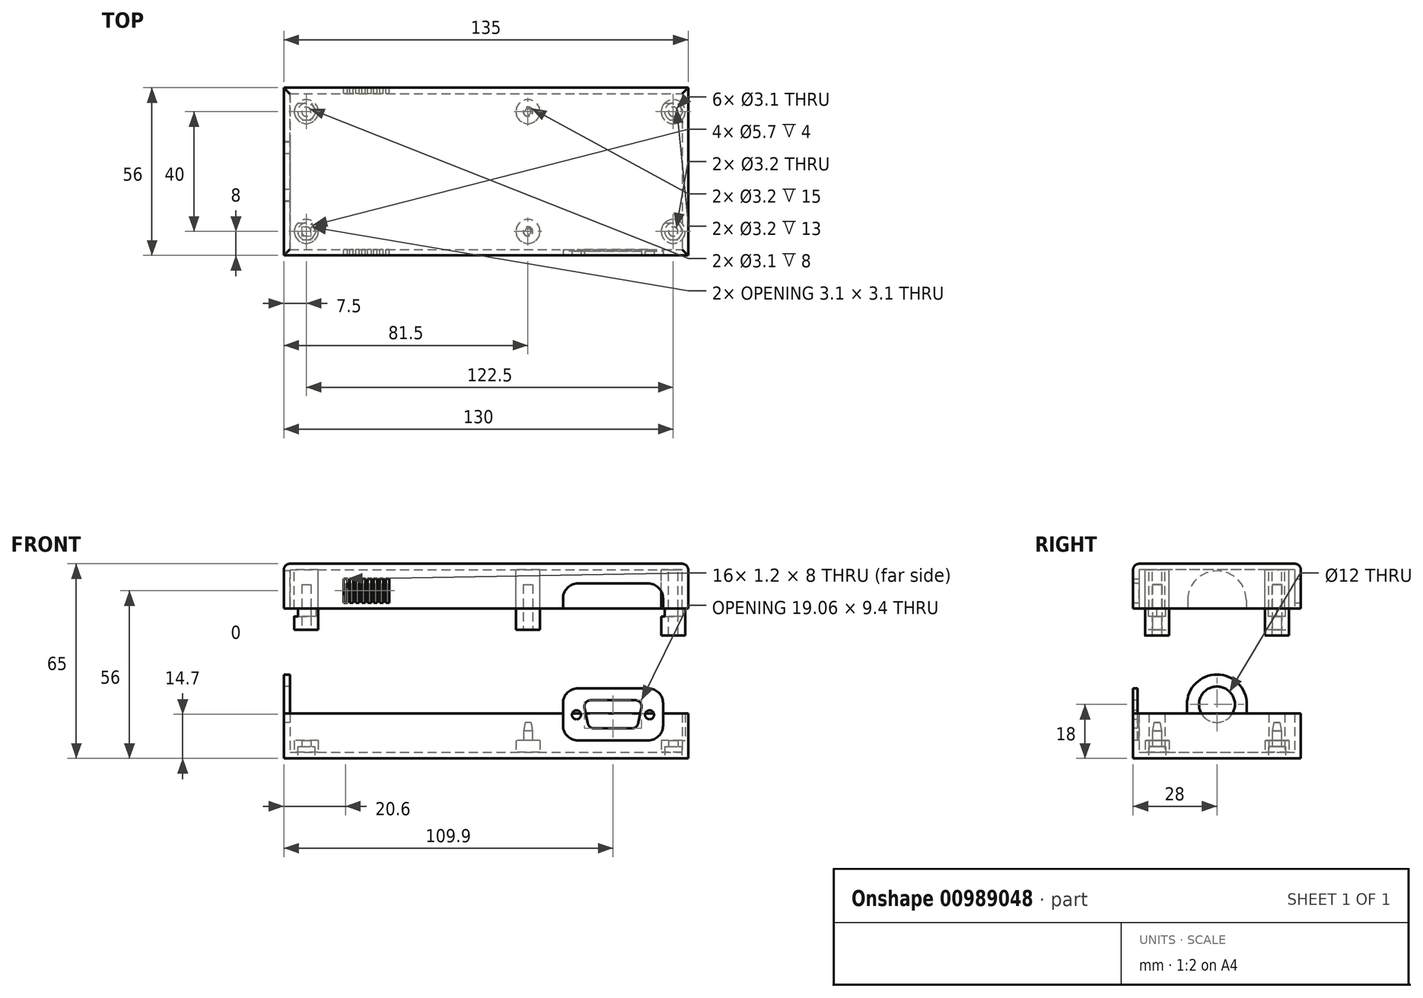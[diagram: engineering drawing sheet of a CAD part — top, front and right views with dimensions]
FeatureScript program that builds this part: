
annotation { "Feature Type Name" : "Feature", "Feature Type Description" : "" }
export const myFeature = defineFeature(function(context is Context, id is Id, definition is map)
    precondition{}
    {
        {
            var Q0;
            Q0=qCreatedBy(makeId("Top.planeOp"),FACE);
            var sketch = newSketch(context, id + "F0", { "sketchPlane" : qUnion([Q0])});
            skLineSegment(sketch, "E0.bottom", {"start": v(0, 0) * mm, "end": v(135, 0) * mm});
            skLineSegment(sketch, "E0.top", {"start": v(0, 56) * mm, "end": v(135, 56) * mm});
            skLineSegment(sketch, "E0.left", {"start": v(0, 0) * mm, "end": v(0, 56) * mm});
            skLineSegment(sketch, "E0.right", {"start": v(135, 0) * mm, "end": v(135, 56) * mm});
            skSolve(sketch);
        }
        {
            var Q0;
            Q0=makeQuery(id+"F0.imprint","IMPRINT",FACE,{"disambiguationData":[TD([[makeQuery(id+"F0.imprint","IMPRINT",EDGE,{"derivedFrom":sQuery(id+"F0.wireOp",EDGE,"E0.bottom")}),1.0]])]});
            extrude(context, id + "F1", {"entities" : qUnion([Q0]), "depth" : 15 * mm, "offsetDistance" : 25 * mm});
        }
        {
            var Q0;
            Q0=makeQuery(id+"F1.opExtrude","CAP_FACE",FACE,{"disambiguationData":[OSD([sQuery(id+"F0.wireOp",EDGE,"E0.bottom"),sQuery(id+"F0.wireOp",EDGE,"E0.top"),sQuery(id+"F0.wireOp",EDGE,"E0.left"),sQuery(id+"F0.wireOp",EDGE,"E0.right")])],"isStart":false});
            shell(context, id + "F2", {"entities" : qUnion([Q0]), "thickness" : 2 * mm});
        }
        {
            var Q0;
            Q0=makeQuery(id+"F2.opShell","OFFSET_FACE",FACE,{"disambiguationData":[OSD([sQuery(id+"F0.wireOp",EDGE,"E0.bottom"),sQuery(id+"F0.wireOp",EDGE,"E0.top"),sQuery(id+"F0.wireOp",EDGE,"E0.left"),sQuery(id+"F0.wireOp",EDGE,"E0.right")])]});
            var sketch = newSketch(context, id + "F3", { "sketchPlane" : qUnion([Q0])});
            skLineSegment(sketch, "E1.bottom", {"start": v(2.5, 53) * mm, "end": v(86.5, 53) * mm, "construction": true});
            skLineSegment(sketch, "E1.top", {"start": v(2.5, 3) * mm, "end": v(86.5, 3) * mm, "construction": true});
            skLineSegment(sketch, "E1.left", {"start": v(2.5, 53) * mm, "end": v(2.5, 3) * mm, "construction": true});
            skLineSegment(sketch, "E1.right", {"start": v(86.5, 53) * mm, "end": v(86.5, 3) * mm, "construction": true});
            skCircle(sketch, "E2", {"center": v(81.5, 48) * mm, "radius": 1.5 * mm});
            skCircle(sketch, "E3", {"center": v(81.5, 8) * mm, "radius": 1.5 * mm});
            skCircle(sketch, "E4", {"center": v(7.5, 8) * mm, "radius": 1.5 * mm});
            skCircle(sketch, "E5", {"center": v(7.5, 48) * mm, "radius": 1.5 * mm});
            skSolve(sketch);
        }
        {
            var Q0;
            Q0=qSketchRegion(id+"F3",true);
            extrude(context, id + "F4", {"entities" : qUnion([Q0]), "operationType" : NewBodyOperationType.ADD, "depth" : 10 * mm, "offsetDistance" : 25 * mm});
        }
        {
            var Q0;
            Q0=makeQuery(id+"F2.opShell","OFFSET_FACE",FACE,{"disambiguationData":[OSD([sQuery(id+"F0.wireOp",EDGE,"E0.bottom"),sQuery(id+"F0.wireOp",EDGE,"E0.top"),sQuery(id+"F0.wireOp",EDGE,"E0.left"),sQuery(id+"F0.wireOp",EDGE,"E0.right")])]});
            var sketch = newSketch(context, id + "F5", { "sketchPlane" : qUnion([Q0])});
            skCircle(sketch, "E6", {"center": v(81.5, 48) * mm, "radius": 4 * mm});
            skCircle(sketch, "E7", {"center": v(81.5, 8) * mm, "radius": 4 * mm});
            skCircle(sketch, "E8", {"center": v(7.5, 48) * mm, "radius": 4 * mm});
            skCircle(sketch, "E9", {"center": v(7.5, 8) * mm, "radius": 4 * mm});
            skSolve(sketch);
        }
        {
            var Q0;
            Q0=qSketchRegion(id+"F5",true);
            extrude(context, id + "F6", {"entities" : qUnion([Q0]), "operationType" : NewBodyOperationType.ADD, "depth" : 4 * mm, "offsetDistance" : 25 * mm});
        }
        {
            var Q0;
            Q0=qCreatedBy(makeId("Top.planeOp"),FACE);
            cPlane(context, id + "F7", {"entities" : qUnion([Q0]), "cplaneType" : CPlaneType.OFFSET, "offset" : 50 * mm, "width" : 150 * mm, "height" : 150 * mm});
        }
        {
            var Q0;
            Q0=makeQuery(id+"F1.opExtrude","SWEPT_FACE",FACE,{"disambiguationData":[OSD([sQuery(id+"F0.wireOp",EDGE,"E0.bottom")])]});
            var sketch = newSketch(context, id + "F8", { "sketchPlane" : qUnion([Q0])});
            skLineSegment(sketch, "E10", {"start": v(102.37, 19.4) * mm, "end": v(117.43, 19.4) * mm});
            skLineSegment(sketch, "E11", {"start": v(119.39, 16.98) * mm, "end": v(118.24, 11.58) * mm});
            skLineSegment(sketch, "E12", {"start": v(116.28, 10) * mm, "end": v(103.52, 10) * mm});
            skLineSegment(sketch, "E13", {"start": v(101.56, 11.58) * mm, "end": v(100.41, 16.98) * mm});
            skPoint(sketch, "E14.visualSharp", {"position": v(99.9, 19.4) * mm});
            skArc(sketch, "E14.filletArc", {"start": v(102.37, 19.4) * mm, "mid": v(100.82, 18.66) * mm, "end": v(100.41, 16.98) * mm});
            skPoint(sketch, "E15.visualSharp", {"position": v(119.9, 19.4) * mm});
            skArc(sketch, "E15.filletArc", {"start": v(119.39, 16.98) * mm, "mid": v(118.98, 18.66) * mm, "end": v(117.43, 19.4) * mm});
            skPoint(sketch, "E16.visualSharp", {"position": v(117.9, 10) * mm});
            skArc(sketch, "E16.filletArc", {"start": v(116.28, 10) * mm, "mid": v(117.54, 10.45) * mm, "end": v(118.24, 11.58) * mm});
            skPoint(sketch, "E17.visualSharp", {"position": v(101.9, 10) * mm});
            skArc(sketch, "E17.filletArc", {"start": v(101.56, 11.58) * mm, "mid": v(102.26, 10.45) * mm, "end": v(103.52, 10) * mm});
            skCircle(sketch, "E18", {"center": v(97.7, 14.53) * mm, "radius": 1.5 * mm});
            skCircle(sketch, "E19", {"center": v(122.1, 14.53) * mm, "radius": 1.5 * mm});
            skLineSegment(sketch, "E20", {"start": v(109.9, 25.37) * mm, "end": v(109.9, 5.82) * mm, "construction": true});
            skLineSegment(sketch, "E21.bottom", {"start": v(98.2, 23.4) * mm, "end": v(121.6, 23.4) * mm});
            skLineSegment(sketch, "E21.top", {"start": v(98.2, 6) * mm, "end": v(121.6, 6) * mm});
            skLineSegment(sketch, "E21.left", {"start": v(93.2, 18.4) * mm, "end": v(93.2, 11) * mm});
            skLineSegment(sketch, "E21.right", {"start": v(126.6, 18.4) * mm, "end": v(126.6, 11) * mm});
            skPoint(sketch, "E22.visualSharp", {"position": v(126.6, 6) * mm});
            skArc(sketch, "E22.filletArc", {"start": v(121.6, 6) * mm, "mid": v(125.14, 7.46) * mm, "end": v(126.6, 11) * mm});
            skPoint(sketch, "E23.visualSharp", {"position": v(93.2, 6) * mm});
            skArc(sketch, "E23.filletArc", {"start": v(93.2, 11) * mm, "mid": v(94.66, 7.46) * mm, "end": v(98.2, 6) * mm});
            skPoint(sketch, "E24.visualSharp", {"position": v(126.6, 23.4) * mm});
            skArc(sketch, "E24.filletArc", {"start": v(126.6, 18.4) * mm, "mid": v(125.14, 21.94) * mm, "end": v(121.6, 23.4) * mm});
            skPoint(sketch, "E25.visualSharp", {"position": v(93.2, 23.4) * mm});
            skArc(sketch, "E25.filletArc", {"start": v(98.2, 23.4) * mm, "mid": v(94.66, 21.94) * mm, "end": v(93.2, 18.4) * mm});
            skSolve(sketch);
        }
        {
            var Q0;
            Q0=makeQuery(id+"F8.imprint","IMPRINT",FACE,{"disambiguationData":[TD([[makeQuery(id+"F8.imprint","IMPRINT",EDGE,{"derivedFrom":sQuery(id+"F8.wireOp",EDGE,"E12")}),1.0]])]});
            var sketch = newSketch(context, id + "F9", { "sketchPlane" : qUnion([Q0])});
            skLineSegment(sketch, "E26.bottom", {"start": v(93.2, 23.4) * mm, "end": v(126.6, 23.4) * mm});
            skLineSegment(sketch, "E26.top", {"start": v(98.2, 6) * mm, "end": v(121.6, 6) * mm});
            skLineSegment(sketch, "E26.left", {"start": v(93.2, 23.4) * mm, "end": v(93.2, 11) * mm});
            skLineSegment(sketch, "E26.right", {"start": v(126.6, 23.4) * mm, "end": v(126.6, 11) * mm});
            skPoint(sketch, "E27.visualSharp", {"position": v(93.2, 6) * mm});
            skArc(sketch, "E27.filletArc", {"start": v(93.2, 11) * mm, "mid": v(94.66, 7.46) * mm, "end": v(98.2, 6) * mm});
            skPoint(sketch, "E28.visualSharp", {"position": v(126.6, 6) * mm});
            skArc(sketch, "E28.filletArc", {"start": v(121.6, 6) * mm, "mid": v(125.14, 7.46) * mm, "end": v(126.6, 11) * mm});
            skSolve(sketch);
        }
        {
            var Q0;
            Q0=qSketchRegion(id+"F9",true);
            extrude(context, id + "F10", {"entities" : qUnion([Q0]), "operationType" : NewBodyOperationType.REMOVE, "oppositeDirection" : true, "depth" : 5 * mm, "offsetDistance" : 25 * mm});
        }
        {
            var Q0;
            Q0=qSketchRegion(id+"F8",true);
            extrude(context, id + "F11", {"entities" : qUnion([Q0]), "oppositeDirection" : true, "depth" : 1.5 * mm, "offsetDistance" : 25 * mm});
        }
        {
            var Q0;
            Q0=makeQuery(id+"F1.opExtrude","SWEPT_FACE",FACE,{"disambiguationData":[OSD([sQuery(id+"F0.wireOp",EDGE,"E0.left")])]});
            var sketch = newSketch(context, id + "F12", { "sketchPlane" : qUnion([Q0])});
            skCircle(sketch, "E29", {"center": v(-28, 18) * mm, "radius": 6 * mm});
            skSolve(sketch);
        }
        {
            var Q0;
            {var subQ0=sQuery(id+"F12.wireOp",EDGE,"E29");var subQ1=makeQuery(id+"F1.opExtrude","CAP_EDGE",EDGE,{"disambiguationData":[OSD([sQuery(id+"F0.wireOp",EDGE,"E0.left")])],"isStart":false});var subQ2=makeQuery(id+"F12.imprint","INTERSECT",VERTEX,{"disambiguationData":[OD(0.0)],"derivedFrom":[subQ1,subQ0]});Q0=makeQuery(id+"F12.imprint","IMPRINT",FACE,{"disambiguationData":[TD([[makeQuery(id+"F12.imprint","IMPRINT",EDGE,{"disambiguationData":[TD([[subQ2,1.0]])],"derivedFrom":subQ0}),1.0]])]});}
            extrude(context, id + "F13", {"entities" : qUnion([Q0]), "operationType" : NewBodyOperationType.REMOVE, "oppositeDirection" : true, "depth" : 25 * mm, "offsetDistance" : 25 * mm});
        }
        {
            var Q0;
            Q0=makeQuery(id+"F1.opExtrude","SWEPT_FACE",FACE,{"disambiguationData":[OSD([sQuery(id+"F0.wireOp",EDGE,"E0.left")])]});
            var sketch = newSketch(context, id + "F14", { "sketchPlane" : qUnion([Q0])});
            skCircle(sketch, "E30", {"center": v(-28, 18) * mm, "radius": 6 * mm});
            skArc(sketch, "E31", {"start": v(-18, 18) * mm, "mid": v(-28, 28) * mm, "end": v(-38, 18) * mm});
            skLineSegment(sketch, "E32.top", {"start": v(-38, 8) * mm, "end": v(-18, 8) * mm});
            skLineSegment(sketch, "E32.left", {"start": v(-38, 18) * mm, "end": v(-38, 8) * mm});
            skLineSegment(sketch, "E32.right", {"start": v(-18, 18) * mm, "end": v(-18, 8) * mm});
            skSolve(sketch);
        }
        {
            var Q0;
            {var subQ0=sQuery(id+"F14.wireOp",EDGE,"E30");var subQ1=sQuery(id+"F0.wireOp",EDGE,"E0.bottom");var subQ2=sQuery(id+"F0.wireOp",EDGE,"E0.left");var subQ7=makeQuery(id+"F1.opExtrude","CAP_EDGE",EDGE,{"disambiguationData":[OSD([subQ2])],"isStart":false});var subQ8=makeQuery(id+"F13.boolean.opBoolean","SPLIT",EDGE,{"disambiguationData":[TD([makeQuery(id+"F1.opExtrude","SWEPT_FACE",FACE,{"disambiguationData":[OSD([subQ1])]})])],"derivedFrom":subQ7});var subQ9=makeQuery(id+"F14.imprint","INTERSECT",VERTEX,{"derivedFrom":[subQ8,subQ0]});Q0=makeQuery(id+"F14.imprint","IMPRINT",FACE,{"disambiguationData":[TD([[makeQuery(id+"F14.imprint","IMPRINT",EDGE,{"disambiguationData":[TD([[subQ9,-1.0]])],"derivedFrom":subQ0}),-1.0]])]});}
            extrude(context, id + "F15", {"entities" : qUnion([Q0]), "operationType" : NewBodyOperationType.ADD, "oppositeDirection" : true, "depth" : 2 * mm, "offsetDistance" : 25 * mm});
        }
        {
            var Q0;
            Q0=qCreatedBy(id+"F7.planeOp",FACE);
            var sketch = newSketch(context, id + "F16", { "sketchPlane" : qUnion([Q0])});
            skLineSegment(sketch, "E33.bottom", {"start": v(0, 56) * mm, "end": v(135, 56) * mm});
            skLineSegment(sketch, "E33.top", {"start": v(0, 0) * mm, "end": v(135, 0) * mm});
            skLineSegment(sketch, "E33.left", {"start": v(0, 56) * mm, "end": v(0, 0) * mm});
            skLineSegment(sketch, "E33.right", {"start": v(135, 56) * mm, "end": v(135, 0) * mm});
            skSolve(sketch);
        }
        {
            var Q0;
            Q0=makeQuery(id+"F16.imprint","IMPRINT",FACE,{"disambiguationData":[TD([[makeQuery(id+"F16.imprint","IMPRINT",EDGE,{"derivedFrom":sQuery(id+"F16.wireOp",EDGE,"E33.bottom")}),-1.0]])]});
            extrude(context, id + "F17", {"entities" : qUnion([Q0]), "depth" : 15 * mm, "offsetDistance" : 25 * mm});
        }
        {
            var Q0;
            Q0=makeQuery(id+"F17.opExtrude","CAP_FACE",FACE,{"disambiguationData":[OSD([sQuery(id+"F16.wireOp",EDGE,"E33.bottom"),sQuery(id+"F16.wireOp",EDGE,"E33.top"),sQuery(id+"F16.wireOp",EDGE,"E33.left"),sQuery(id+"F16.wireOp",EDGE,"E33.right")])],"isStart":true});
            shell(context, id + "F18", {"entities" : qUnion([Q0]), "thickness" : 2 * mm});
        }
        {
            var Q0;
            Q0=makeQuery(id+"F17.opExtrude","SWEPT_FACE",FACE,{"disambiguationData":[OSD([sQuery(id+"F16.wireOp",EDGE,"E33.left")])]});
            var sketch = newSketch(context, id + "F19", { "sketchPlane" : qUnion([Q0])});
            skArc(sketch, "E34", {"start": v(-18.2, 52.8) * mm, "mid": v(-28, 62.6) * mm, "end": v(-37.8, 52.8) * mm});
            skPoint(sketch, "E34.centerSnap0", {"position": v(-28, 50) * mm});
            skLineSegment(sketch, "E35.top", {"start": v(-37.8, 43) * mm, "end": v(-18.2, 43) * mm});
            skLineSegment(sketch, "E35.left", {"start": v(-37.8, 52.8) * mm, "end": v(-37.8, 43) * mm});
            skLineSegment(sketch, "E35.right", {"start": v(-18.2, 52.8) * mm, "end": v(-18.2, 43) * mm});
            skSolve(sketch);
        }
        {
            var Q0;
            {var subQ0=sQuery(id+"F19.wireOp",EDGE,"E34");var subQ1=makeQuery(id+"F17.opExtrude","CAP_EDGE",EDGE,{"disambiguationData":[OSD([sQuery(id+"F16.wireOp",EDGE,"E33.left")])],"isStart":true});var subQ2=makeQuery(id+"F19.imprint","INTERSECT",VERTEX,{"disambiguationData":[OD(0.0)],"derivedFrom":[subQ1,subQ0]});Q0=makeQuery(id+"F19.imprint","IMPRINT",FACE,{"disambiguationData":[TD([[makeQuery(id+"F19.imprint","IMPRINT",EDGE,{"disambiguationData":[TD([[subQ2,1.0]])],"derivedFrom":subQ0}),1.0]])]});}
            extrude(context, id + "F20", {"entities" : qUnion([Q0]), "operationType" : NewBodyOperationType.REMOVE, "oppositeDirection" : true, "depth" : 5 * mm, "offsetDistance" : 25 * mm});
        }
        {
            var Q0;
            Q0=makeQuery(id+"F17.opExtrude","SWEPT_FACE",FACE,{"disambiguationData":[OSD([sQuery(id+"F16.wireOp",EDGE,"E33.top")])]});
            var sketch = newSketch(context, id + "F21", { "sketchPlane" : qUnion([Q0])});
            skLineSegment(sketch, "E36.bottom", {"start": v(93.2, 50) * mm, "end": v(126.6, 50) * mm});
            skLineSegment(sketch, "E36.top", {"start": v(98.2, 58.4) * mm, "end": v(121.6, 58.4) * mm});
            skLineSegment(sketch, "E36.left", {"start": v(93.2, 50) * mm, "end": v(93.2, 53.4) * mm});
            skLineSegment(sketch, "E36.right", {"start": v(126.6, 50) * mm, "end": v(126.6, 53.4) * mm});
            skPoint(sketch, "E37.visualSharp", {"position": v(93.2, 58.4) * mm});
            skArc(sketch, "E37.filletArc", {"start": v(98.2, 58.4) * mm, "mid": v(94.66, 56.94) * mm, "end": v(93.2, 53.4) * mm});
            skPoint(sketch, "E38.visualSharp", {"position": v(126.6, 58.4) * mm});
            skArc(sketch, "E38.filletArc", {"start": v(126.6, 53.4) * mm, "mid": v(125.14, 56.94) * mm, "end": v(121.6, 58.4) * mm});
            skSolve(sketch);
        }
        {
            var Q0;
            Q0=makeQuery(id+"F21.imprint","IMPRINT",FACE,{"disambiguationData":[TD([[makeQuery(id+"F21.imprint","IMPRINT",EDGE,{"derivedFrom":sQuery(id+"F21.wireOp",EDGE,"E36.bottom")}),1.0]])]});
            extrude(context, id + "F22", {"entities" : qUnion([Q0]), "operationType" : NewBodyOperationType.REMOVE, "oppositeDirection" : true, "depth" : 5 * mm, "offsetDistance" : 25 * mm});
        }
        {
            var Q0;
            Q0=makeQuery(id+"F17.opExtrude","CAP_FACE",FACE,{"disambiguationData":[OSD([sQuery(id+"F16.wireOp",EDGE,"E33.bottom"),sQuery(id+"F16.wireOp",EDGE,"E33.top"),sQuery(id+"F16.wireOp",EDGE,"E33.left"),sQuery(id+"F16.wireOp",EDGE,"E33.right")])],"isStart":false});
            fillet(context, id + "F23", {"entities" : qUnion([Q0]), "radius" : 2 * mm, "tangentPropagation" : true, "allowEdgeOverflow" : false});
        }
        {
            var Q0;
            Q0=makeQuery(id+"F18.opShell","OFFSET_FACE",FACE,{"disambiguationData":[OSD([sQuery(id+"F16.wireOp",EDGE,"E33.bottom"),sQuery(id+"F16.wireOp",EDGE,"E33.top"),sQuery(id+"F16.wireOp",EDGE,"E33.left"),sQuery(id+"F16.wireOp",EDGE,"E33.right")])]});
            var sketch = newSketch(context, id + "F24", { "sketchPlane" : qUnion([Q0])});
            skCircle(sketch, "E39", {"center": v(81.5, -48) * mm, "radius": 4 * mm});
            skCircle(sketch, "E40", {"center": v(81.5, -8) * mm, "radius": 4 * mm});
            skCircle(sketch, "E41", {"center": v(7.5, -48) * mm, "radius": 4 * mm});
            skCircle(sketch, "E42", {"center": v(7.5, -8) * mm, "radius": 4 * mm});
            skSolve(sketch);
        }
        {
            var Q0;
            Q0 = qSketchRegion(id + "F24", true);
            extrude(context, id + "F25", {"entities" : qUnion([Q0]), "operationType" : NewBodyOperationType.ADD, "depth" : 20 * mm, "offsetDistance" : 25 * mm});
        }
        {
            var Q0;
            Q0=makeQuery(id+"F25.opExtrude","CAP_FACE",FACE,{"disambiguationData":[OSD([sQuery(id+"F24.wireOp",EDGE,"E40")])],"isStart":false});
            var sketch = newSketch(context, id + "F26", { "sketchPlane" : qUnion([Q0])});
            skCircle(sketch, "E43", {"center": v(81.5, -8) * mm, "radius": 1.6 * mm});
            skCircle(sketch, "E44", {"center": v(7.5, -8) * mm, "radius": 1.55 * mm});
            skCircle(sketch, "E45", {"center": v(7.5, -48) * mm, "radius": 1.55 * mm});
            skCircle(sketch, "E46", {"center": v(81.5, -48) * mm, "radius": 1.6 * mm});
            skSolve(sketch);
        }
        {
            var Q0;
            Q0 = qSketchRegion(id + "F26", true);
            extrude(context, id + "F27", {"entities" : qUnion([Q0]), "operationType" : NewBodyOperationType.REMOVE, "oppositeDirection" : true, "depth" : 15 * mm, "offsetDistance" : 25 * mm});
        }
        {
            var Q0;
            Q0=makeQuery(id+"F17.opExtrude","SWEPT_FACE",FACE,{"disambiguationData":[OSD([sQuery(id+"F16.wireOp",EDGE,"E33.bottom")])]});
            var sketch = newSketch(context, id + "F28", { "sketchPlane" : qUnion([Q0])});
            skLineSegment(sketch, "E47.bottom", {"start": v(-21.2, 60) * mm, "end": v(-20, 60) * mm});
            skLineSegment(sketch, "E47.top", {"start": v(-21.2, 52) * mm, "end": v(-20, 52) * mm});
            skLineSegment(sketch, "E47.left", {"start": v(-21.2, 60) * mm, "end": v(-21.2, 52) * mm});
            skLineSegment(sketch, "E47.right", {"start": v(-20, 60) * mm, "end": v(-20, 52) * mm});
            skLineSegment(sketch, "E48.1.0.0", {"start": v(-23.2, 60) * mm, "end": v(-23.2, 52) * mm});
            skLineSegment(sketch, "E48.1.0.1", {"start": v(-22, 60) * mm, "end": v(-22, 52) * mm});
            skLineSegment(sketch, "E48.1.0.2", {"start": v(-23.2, 52) * mm, "end": v(-22, 52) * mm});
            skLineSegment(sketch, "E48.1.0.3", {"start": v(-23.2, 60) * mm, "end": v(-22, 60) * mm});
            skLineSegment(sketch, "E48.2.0.0", {"start": v(-25.2, 60) * mm, "end": v(-25.2, 52) * mm});
            skLineSegment(sketch, "E48.2.0.1", {"start": v(-24, 60) * mm, "end": v(-24, 52) * mm});
            skLineSegment(sketch, "E48.2.0.2", {"start": v(-25.2, 52) * mm, "end": v(-24, 52) * mm});
            skLineSegment(sketch, "E48.2.0.3", {"start": v(-25.2, 60) * mm, "end": v(-24, 60) * mm});
            skLineSegment(sketch, "E48.3.0.0", {"start": v(-27.2, 60) * mm, "end": v(-27.2, 52) * mm});
            skLineSegment(sketch, "E48.3.0.1", {"start": v(-26, 60) * mm, "end": v(-26, 52) * mm});
            skLineSegment(sketch, "E48.3.0.2", {"start": v(-27.2, 52) * mm, "end": v(-26, 52) * mm});
            skLineSegment(sketch, "E48.3.0.3", {"start": v(-27.2, 60) * mm, "end": v(-26, 60) * mm});
            skLineSegment(sketch, "E48.4.0.0", {"start": v(-29.2, 60) * mm, "end": v(-29.2, 52) * mm});
            skLineSegment(sketch, "E48.4.0.1", {"start": v(-28, 60) * mm, "end": v(-28, 52) * mm});
            skLineSegment(sketch, "E48.4.0.2", {"start": v(-29.2, 52) * mm, "end": v(-28, 52) * mm});
            skLineSegment(sketch, "E48.4.0.3", {"start": v(-29.2, 60) * mm, "end": v(-28, 60) * mm});
            skLineSegment(sketch, "E48.5.0.0", {"start": v(-31.2, 60) * mm, "end": v(-31.2, 52) * mm});
            skLineSegment(sketch, "E48.5.0.1", {"start": v(-30, 60) * mm, "end": v(-30, 52) * mm});
            skLineSegment(sketch, "E48.5.0.2", {"start": v(-31.2, 52) * mm, "end": v(-30, 52) * mm});
            skLineSegment(sketch, "E48.5.0.3", {"start": v(-31.2, 60) * mm, "end": v(-30, 60) * mm});
            skLineSegment(sketch, "E48.6.0.0", {"start": v(-33.2, 60) * mm, "end": v(-33.2, 52) * mm});
            skLineSegment(sketch, "E48.6.0.1", {"start": v(-32, 60) * mm, "end": v(-32, 52) * mm});
            skLineSegment(sketch, "E48.6.0.2", {"start": v(-33.2, 52) * mm, "end": v(-32, 52) * mm});
            skLineSegment(sketch, "E48.6.0.3", {"start": v(-33.2, 60) * mm, "end": v(-32, 60) * mm});
            skLineSegment(sketch, "E48.7.0.0", {"start": v(-35.2, 60) * mm, "end": v(-35.2, 52) * mm});
            skLineSegment(sketch, "E48.7.0.1", {"start": v(-34, 60) * mm, "end": v(-34, 52) * mm});
            skLineSegment(sketch, "E48.7.0.2", {"start": v(-35.2, 52) * mm, "end": v(-34, 52) * mm});
            skLineSegment(sketch, "E48.7.0.3", {"start": v(-35.2, 60) * mm, "end": v(-34, 60) * mm});
            skLineSegment(sketch, "E48.direction1", {"start": v(-21.2, 52) * mm, "end": v(-23.2, 52) * mm, "construction": true});
            skSolve(sketch);
        }
        {
            var Q0;
            Q0 = qSketchRegion(id + "F28", true);
            extrude(context, id + "F29", {"entities" : qUnion([Q0]), "operationType" : NewBodyOperationType.REMOVE, "oppositeDirection" : true, "depth" : 100 * mm, "offsetDistance" : 25 * mm});
        }
        {
            var Q0;
            Q0=makeQuery(id+"F1.opExtrude","CAP_FACE",FACE,{"disambiguationData":[OSD([sQuery(id+"F0.wireOp",EDGE,"E0.bottom"),sQuery(id+"F0.wireOp",EDGE,"E0.top"),sQuery(id+"F0.wireOp",EDGE,"E0.left"),sQuery(id+"F0.wireOp",EDGE,"E0.right")])],"isStart":true});
            var sketch = newSketch(context, id + "F30", { "sketchPlane" : qUnion([Q0])});
            skCircle(sketch, "E49", {"center": v(7.5, -48) * mm, "radius": 1.55 * mm});
            skCircle(sketch, "E50", {"center": v(7.5, -8) * mm, "radius": 1.55 * mm});
            skCircle(sketch, "E51", {"center": v(130, -48) * mm, "radius": 1.55 * mm});
            skCircle(sketch, "E52", {"center": v(130, -8) * mm, "radius": 1.55 * mm});
            skSolve(sketch);
        }
        {
            var Q0;
            Q0=makeQuery(id+"F2.opShell","OFFSET_FACE",FACE,{"disambiguationData":[OSD([sQuery(id+"F0.wireOp",EDGE,"E0.bottom"),sQuery(id+"F0.wireOp",EDGE,"E0.top"),sQuery(id+"F0.wireOp",EDGE,"E0.left"),sQuery(id+"F0.wireOp",EDGE,"E0.right")])]});
            var sketch = newSketch(context, id + "F31", { "sketchPlane" : qUnion([Q0])});
            skCircle(sketch, "E53", {"center": v(130, 48) * mm, "radius": 4 * mm});
            skCircle(sketch, "E54", {"center": v(130, 8) * mm, "radius": 4 * mm});
            skSolve(sketch);
        }
        {
            var Q0;
            Q0 = qSketchRegion(id + "F31", true);
            extrude(context, id + "F32", {"entities" : qUnion([Q0]), "operationType" : NewBodyOperationType.ADD, "depth" : 4 * mm, "offsetDistance" : 25 * mm});
        }
        {
            var Q0;
            Q0 = qSketchRegion(id + "F30", true);
            extrude(context, id + "F33", {"entities" : qUnion([Q0]), "operationType" : NewBodyOperationType.REMOVE, "oppositeDirection" : true, "depth" : 25 * mm, "offsetDistance" : 25 * mm});
        }
        {
            var Q0;
            Q0=makeQuery(id+"F1.opExtrude","CAP_FACE",FACE,{"disambiguationData":[OSD([sQuery(id+"F0.wireOp",EDGE,"E0.bottom"),sQuery(id+"F0.wireOp",EDGE,"E0.top"),sQuery(id+"F0.wireOp",EDGE,"E0.left"),sQuery(id+"F0.wireOp",EDGE,"E0.right")])],"isStart":true});
            var sketch = newSketch(context, id + "F34", { "sketchPlane" : qUnion([Q0])});
            skCircle(sketch, "E55", {"center": v(7.5, -8) * mm, "radius": 2.85 * mm});
            skCircle(sketch, "E56", {"center": v(7.5, -48) * mm, "radius": 2.85 * mm});
            skCircle(sketch, "E57", {"center": v(130, -8) * mm, "radius": 2.85 * mm});
            skCircle(sketch, "E58", {"center": v(130, -48) * mm, "radius": 2.85 * mm});
            skSolve(sketch);
        }
        {
            var Q0;
            Q0 = qSketchRegion(id + "F34", true);
            extrude(context, id + "F35", {"entities" : qUnion([Q0]), "operationType" : NewBodyOperationType.REMOVE, "oppositeDirection" : true, "depth" : 4 * mm, "offsetDistance" : 25 * mm});
        }
        {
            var Q0;
            Q0=makeQuery(id+"F18.opShell","OFFSET_FACE",FACE,{"disambiguationData":[OSD([sQuery(id+"F16.wireOp",EDGE,"E33.bottom"),sQuery(id+"F16.wireOp",EDGE,"E33.top"),sQuery(id+"F16.wireOp",EDGE,"E33.left"),sQuery(id+"F16.wireOp",EDGE,"E33.right")])]});
            var sketch = newSketch(context, id + "F36", { "sketchPlane" : qUnion([Q0])});
            skCircle(sketch, "E59", {"center": v(130, -8) * mm, "radius": 4 * mm});
            skCircle(sketch, "E60", {"center": v(130, -48) * mm, "radius": 4 * mm});
            skSolve(sketch);
        }
        {
            var Q0;
            Q0 = qSketchRegion(id + "F36", true);
            extrude(context, id + "F37", {"entities" : qUnion([Q0]), "operationType" : NewBodyOperationType.ADD, "depth" : 22 * mm, "offsetDistance" : 25 * mm});
        }
        {
            var Q0;
            Q0=makeQuery(id+"F32.opExtrude","CAP_FACE",FACE,{"disambiguationData":[OSD([sQuery(id+"F31.wireOp",EDGE,"E53")])],"isStart":false});
            var sketch = newSketch(context, id + "F38", { "sketchPlane" : qUnion([Q0])});
            skCircle(sketch, "E61", {"center": v(130, 48) * mm, "radius": 4 * mm});
            skCircle(sketch, "E62", {"center": v(130, 8) * mm, "radius": 4 * mm});
            skSolve(sketch);
        }
        {
            var Q0;
            Q0 = qSketchRegion(id + "F38", true);
            extrude(context, id + "F39", {"entities" : qUnion([Q0]), "operationType" : NewBodyOperationType.REMOVE, "depth" : 25 * mm, "offsetDistance" : 25 * mm});
        }
        {
            var Q0;
            Q0=makeQuery(id+"F18.opShell","OFFSET_FACE",FACE,{"disambiguationData":[OSD([sQuery(id+"F16.wireOp",EDGE,"E33.bottom"),sQuery(id+"F16.wireOp",EDGE,"E33.top"),sQuery(id+"F16.wireOp",EDGE,"E33.left"),sQuery(id+"F16.wireOp",EDGE,"E33.right")])]});
            var sketch = newSketch(context, id + "F40", { "sketchPlane" : qUnion([Q0])});
            skCircle(sketch, "E63", {"center": v(130, -8) * mm, "radius": 1.6 * mm});
            skCircle(sketch, "E64", {"center": v(130, -48) * mm, "radius": 1.6 * mm});
            skSolve(sketch);
        }
        {
            var Q0;
            Q0 = qSketchRegion(id + "F40", true);
            extrude(context, id + "F41", {"entities" : qUnion([Q0]), "operationType" : NewBodyOperationType.REMOVE, "depth" : 22 * mm, "offsetDistance" : 25 * mm});
        }
        {
            var Q0;
            Q0=qCreatedBy(id+"F7.planeOp",FACE);
            var sketch = newSketch(context, id + "F42", { "sketchPlane" : qUnion([Q0])});
            skCircle(sketch, "E65.cCircle", {"center": v(7.5, 8) * mm, "radius": 2.85 * mm, "construction": true});
            skLineSegment(sketch, "E65.0", {"start": v(5.85, 10.85) * mm, "end": v(9.15, 10.85) * mm});
            skLineSegment(sketch, "E65.1", {"start": v(9.15, 10.85) * mm, "end": v(10.8, 8) * mm});
            skLineSegment(sketch, "E65.2", {"start": v(10.8, 8) * mm, "end": v(9.15, 5.15) * mm});
            skLineSegment(sketch, "E65.3", {"start": v(9.15, 5.15) * mm, "end": v(5.85, 5.15) * mm});
            skPoint(sketch, "E65.0.midPoint", {"position": v(7.5, 10.85) * mm});
            skLineSegment(sketch, "E66.bottom", {"start": v(5.85, 5.15) * mm, "end": v(2.5, 5.15) * mm});
            skLineSegment(sketch, "E66.top", {"start": v(5.85, 10.85) * mm, "end": v(2.5, 10.85) * mm});
            skLineSegment(sketch, "E66.right", {"start": v(2.5, 5.15) * mm, "end": v(2.5, 10.85) * mm});
            skCircle(sketch, "E67.cCircle", {"center": v(7.5, 48) * mm, "radius": 2.85 * mm, "construction": true});
            skLineSegment(sketch, "E67.0", {"start": v(5.85, 50.85) * mm, "end": v(9.15, 50.85) * mm});
            skLineSegment(sketch, "E67.1", {"start": v(9.15, 50.85) * mm, "end": v(10.8, 48) * mm});
            skLineSegment(sketch, "E67.2", {"start": v(10.8, 48) * mm, "end": v(9.15, 45.15) * mm});
            skLineSegment(sketch, "E67.3", {"start": v(9.15, 45.15) * mm, "end": v(5.85, 45.15) * mm});
            skPoint(sketch, "E67.0.midPoint", {"position": v(7.5, 50.85) * mm});
            skLineSegment(sketch, "E68.bottom", {"start": v(5.85, 45.15) * mm, "end": v(2.5, 45.15) * mm});
            skLineSegment(sketch, "E68.top", {"start": v(5.85, 50.85) * mm, "end": v(2.5, 50.85) * mm});
            skLineSegment(sketch, "E68.right", {"start": v(2.5, 45.15) * mm, "end": v(2.5, 50.85) * mm});
            skCircle(sketch, "E69.cCircle", {"center": v(130, 8) * mm, "radius": 2.85 * mm, "construction": true});
            skLineSegment(sketch, "E69.0", {"start": v(128.35, 10.85) * mm, "end": v(131.65, 10.85) * mm});
            skLineSegment(sketch, "E69.1", {"start": v(131.65, 10.85) * mm, "end": v(133.3, 8) * mm});
            skLineSegment(sketch, "E69.2", {"start": v(133.3, 8) * mm, "end": v(131.65, 5.15) * mm});
            skLineSegment(sketch, "E69.3", {"start": v(131.65, 5.15) * mm, "end": v(128.35, 5.15) * mm});
            skPoint(sketch, "E69.0.midPoint", {"position": v(130, 10.85) * mm});
            skLineSegment(sketch, "E70.bottom", {"start": v(128.35, 5.15) * mm, "end": v(125, 5.15) * mm});
            skLineSegment(sketch, "E70.top", {"start": v(128.35, 10.85) * mm, "end": v(125, 10.85) * mm});
            skLineSegment(sketch, "E70.right", {"start": v(125, 5.15) * mm, "end": v(125, 10.85) * mm});
            skCircle(sketch, "E71.cCircle", {"center": v(130, 48) * mm, "radius": 2.85 * mm, "construction": true});
            skLineSegment(sketch, "E71.0", {"start": v(128.35, 50.85) * mm, "end": v(131.65, 50.85) * mm});
            skLineSegment(sketch, "E71.1", {"start": v(131.65, 50.85) * mm, "end": v(133.3, 48) * mm});
            skLineSegment(sketch, "E71.2", {"start": v(133.3, 48) * mm, "end": v(131.65, 45.15) * mm});
            skLineSegment(sketch, "E71.3", {"start": v(131.65, 45.15) * mm, "end": v(128.35, 45.15) * mm});
            skPoint(sketch, "E71.0.midPoint", {"position": v(130, 50.85) * mm});
            skLineSegment(sketch, "E72.bottom", {"start": v(128.35, 45.15) * mm, "end": v(125, 45.15) * mm});
            skLineSegment(sketch, "E72.top", {"start": v(128.35, 50.85) * mm, "end": v(125, 50.85) * mm});
            skLineSegment(sketch, "E72.right", {"start": v(125, 45.15) * mm, "end": v(125, 50.85) * mm});
            skSolve(sketch);
        }
        {
            var Q0;
            Q0 = qSketchRegion(id + "F42", true);
            extrude(context, id + "F43", {"entities" : qUnion([Q0]), "operationType" : NewBodyOperationType.REMOVE, "oppositeDirection" : true, "depth" : 2.6 * mm, "offsetDistance" : 25 * mm});
        }
        {
            var Q0;
            Q0=makeQuery(id+"F4.opExtrude","CAP_FACE",FACE,{"disambiguationData":[OSD([sQuery(id+"F3.wireOp",EDGE,"E2")])],"isStart":false});
            var Q1;
            Q1=makeQuery(id+"F4.opExtrude","CAP_FACE",FACE,{"disambiguationData":[OSD([sQuery(id+"F3.wireOp",EDGE,"E3")])],"isStart":false});
            chamfer(context, id + "F44", {"entities" : qUnion([Q0, Q1]), "chamferType" : ChamferType.OFFSET_ANGLE, "width" : 0.5 * mm, "oppositeDirection" : false, "angle" : 80 * degree, "tangentPropagation" : true});
        }
    });
